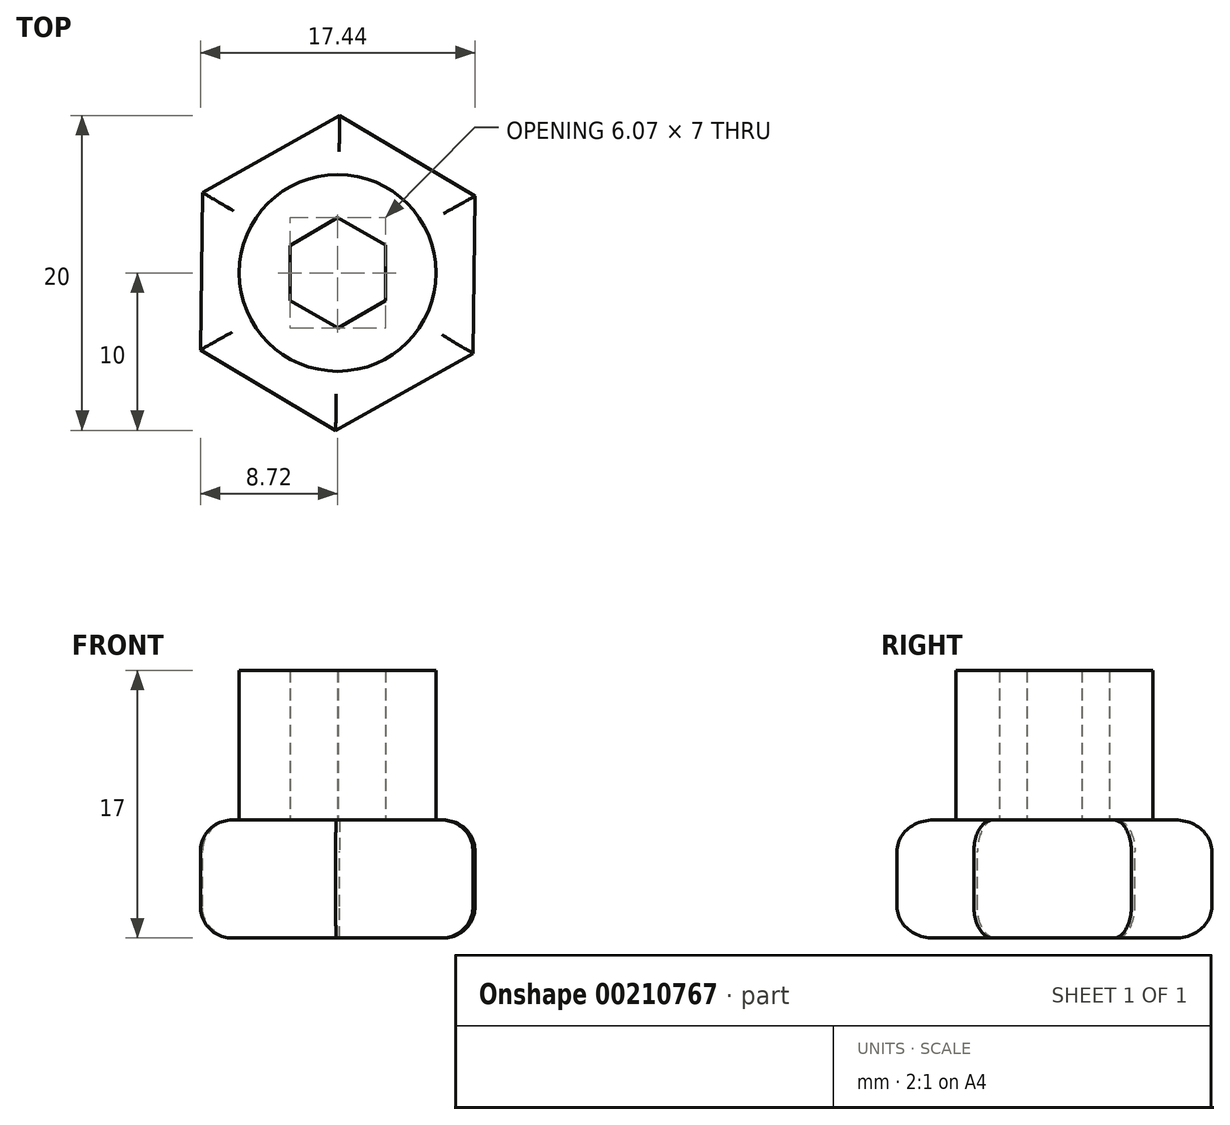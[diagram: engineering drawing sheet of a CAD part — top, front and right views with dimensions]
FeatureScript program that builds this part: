
annotation { "Feature Type Name" : "Feature", "Feature Type Description" : "" }
export const myFeature = defineFeature(function(context is Context, id is Id, definition is map)
    precondition{}
    {
        {
            var Q0;
            Q0=qCreatedBy(makeId("Top.planeOp"),FACE);
            var sketch = newSketch(context, id + "F0", { "sketchPlane" : qUnion([Q0])});
            skCircle(sketch, "E0.cCircle", {"center": v(0, 0) * mm, "radius": 3.03 * mm, "construction": true});
            skLineSegment(sketch, "E0.0", {"start": v(0, 3.5) * mm, "end": v(3.03, 1.76) * mm});
            skLineSegment(sketch, "E0.1", {"start": v(3.03, 1.76) * mm, "end": v(3.04, -1.74) * mm});
            skLineSegment(sketch, "E0.2", {"start": v(3.04, -1.74) * mm, "end": v(0, -3.5) * mm});
            skLineSegment(sketch, "E0.3", {"start": v(0, -3.5) * mm, "end": v(-3.03, -1.76) * mm});
            skLineSegment(sketch, "E0.4", {"start": v(-3.03, -1.76) * mm, "end": v(-3.04, 1.74) * mm});
            skLineSegment(sketch, "E0.5", {"start": v(-3.04, 1.74) * mm, "end": v(0, 3.5) * mm});
            skPoint(sketch, "E0.0.midPoint", {"position": v(1.5, 2.63) * mm});
            skCircle(sketch, "E1", {"center": v(0, 0) * mm, "radius": 6.25 * mm});
            skSolve(sketch);
        }
        {
            var Q0;
            Q0=makeQuery(id+"F0.imprint","IMPRINT",FACE,{"disambiguationData":[TD([[makeQuery(id+"F0.imprint","IMPRINT",EDGE,{"derivedFrom":sQuery(id+"F0.wireOp",EDGE,"E0.0")}),1.0]])]});
            var Q1;
            Q1 = qConstructionFilter(qBodyType(qCreatedBy(id + "F0" ,EDGE), BodyType.WIRE), ConstructionObject.NO);
            extrude(context, id + "F1", {"entities" : qUnion([Q0]), "surfaceEntities" : qUnion([Q1]), "depth" : 9.5 * mm});
        }
        {
            var Q0;
            Q0=qCreatedBy(makeId("Top.planeOp"),FACE);
            var sketch = newSketch(context, id + "F2", { "sketchPlane" : qUnion([Q0])});
            skCircle(sketch, "E2.cCircle", {"center": v(0, 0) * mm, "radius": 8.66 * mm, "construction": true});
            skLineSegment(sketch, "E2.0", {"start": v(0.13, 10) * mm, "end": v(8.72, 4.9) * mm});
            skLineSegment(sketch, "E2.1", {"start": v(8.72, 4.9) * mm, "end": v(8.6, -5.1) * mm});
            skLineSegment(sketch, "E2.2", {"start": v(8.6, -5.1) * mm, "end": v(-0.13, -10) * mm});
            skLineSegment(sketch, "E2.3", {"start": v(-0.13, -10) * mm, "end": v(-8.72, -4.9) * mm});
            skLineSegment(sketch, "E2.4", {"start": v(-8.72, -4.9) * mm, "end": v(-8.6, 5.1) * mm});
            skLineSegment(sketch, "E2.5", {"start": v(-8.6, 5.1) * mm, "end": v(0.13, 10) * mm});
            skPoint(sketch, "E2.0.midPoint", {"position": v(4.42, 7.45) * mm});
            skSolve(sketch);
        }
        {
            var Q0;
            Q0=makeQuery(id+"F2.imprint","IMPRINT",FACE,{"disambiguationData":[TD([[makeQuery(id+"F2.imprint","IMPRINT",EDGE,{"derivedFrom":sQuery(id+"F2.wireOp",EDGE,"E2.0")}),-1.0]])]});
            extrude(context, id + "F3", {"entities" : qUnion([Q0]), "oppositeDirection" : true, "depth" : 7.5 * mm});
        }
        {
            var Q0;
            Q0=makeQuery(id+"F3.opExtrude","CAP_EDGE",EDGE,{"disambiguationData":[OSD([sQuery(id+"F2.wireOp",EDGE,"E2.2")])],"isStart":false});
            var Q1;
            Q1=makeQuery(id+"F3.opExtrude","CAP_EDGE",EDGE,{"disambiguationData":[OSD([sQuery(id+"F2.wireOp",EDGE,"E2.1")])],"isStart":false});
            var Q2;
            Q2=makeQuery(id+"F3.opExtrude","CAP_EDGE",EDGE,{"disambiguationData":[OSD([sQuery(id+"F2.wireOp",EDGE,"E2.5")])],"isStart":false});
            var Q3;
            Q3=makeQuery(id+"F3.opExtrude","CAP_EDGE",EDGE,{"disambiguationData":[OSD([sQuery(id+"F2.wireOp",EDGE,"E2.0")])],"isStart":false});
            var Q4;
            Q4=makeQuery(id+"F3.opExtrude","CAP_EDGE",EDGE,{"disambiguationData":[OSD([sQuery(id+"F2.wireOp",EDGE,"E2.4")])],"isStart":false});
            var Q5;
            Q5=makeQuery(id+"F3.opExtrude","CAP_EDGE",EDGE,{"disambiguationData":[OSD([sQuery(id+"F2.wireOp",EDGE,"E2.3")])],"isStart":false});
            var Q6;
            Q6=makeQuery(id+"F3.opExtrude","CAP_EDGE",EDGE,{"disambiguationData":[OSD([sQuery(id+"F2.wireOp",EDGE,"E2.4")])],"isStart":true});
            var Q7;
            Q7=makeQuery(id+"F3.opExtrude","CAP_EDGE",EDGE,{"disambiguationData":[OSD([sQuery(id+"F2.wireOp",EDGE,"E2.5")])],"isStart":true});
            var Q8;
            Q8=makeQuery(id+"F3.opExtrude","CAP_EDGE",EDGE,{"disambiguationData":[OSD([sQuery(id+"F2.wireOp",EDGE,"E2.3")])],"isStart":true});
            var Q9;
            Q9=makeQuery(id+"F3.opExtrude","CAP_EDGE",EDGE,{"disambiguationData":[OSD([sQuery(id+"F2.wireOp",EDGE,"E2.2")])],"isStart":true});
            var Q10;
            Q10=makeQuery(id+"F3.opExtrude","CAP_EDGE",EDGE,{"disambiguationData":[OSD([sQuery(id+"F2.wireOp",EDGE,"E2.0")])],"isStart":true});
            var Q11;
            Q11=makeQuery(id+"F3.opExtrude","CAP_EDGE",EDGE,{"disambiguationData":[OSD([sQuery(id+"F2.wireOp",EDGE,"E2.1")])],"isStart":true});
            fillet(context, id + "F4", {"entities" : qUnion([Q0, Q1, Q2, Q3, Q4, Q5, Q6, Q7, Q8, Q9, Q10, Q11]), "radius" : 2 * mm, "tangentPropagation" : true, "allowEdgeOverflow" : false});
        }
    });
